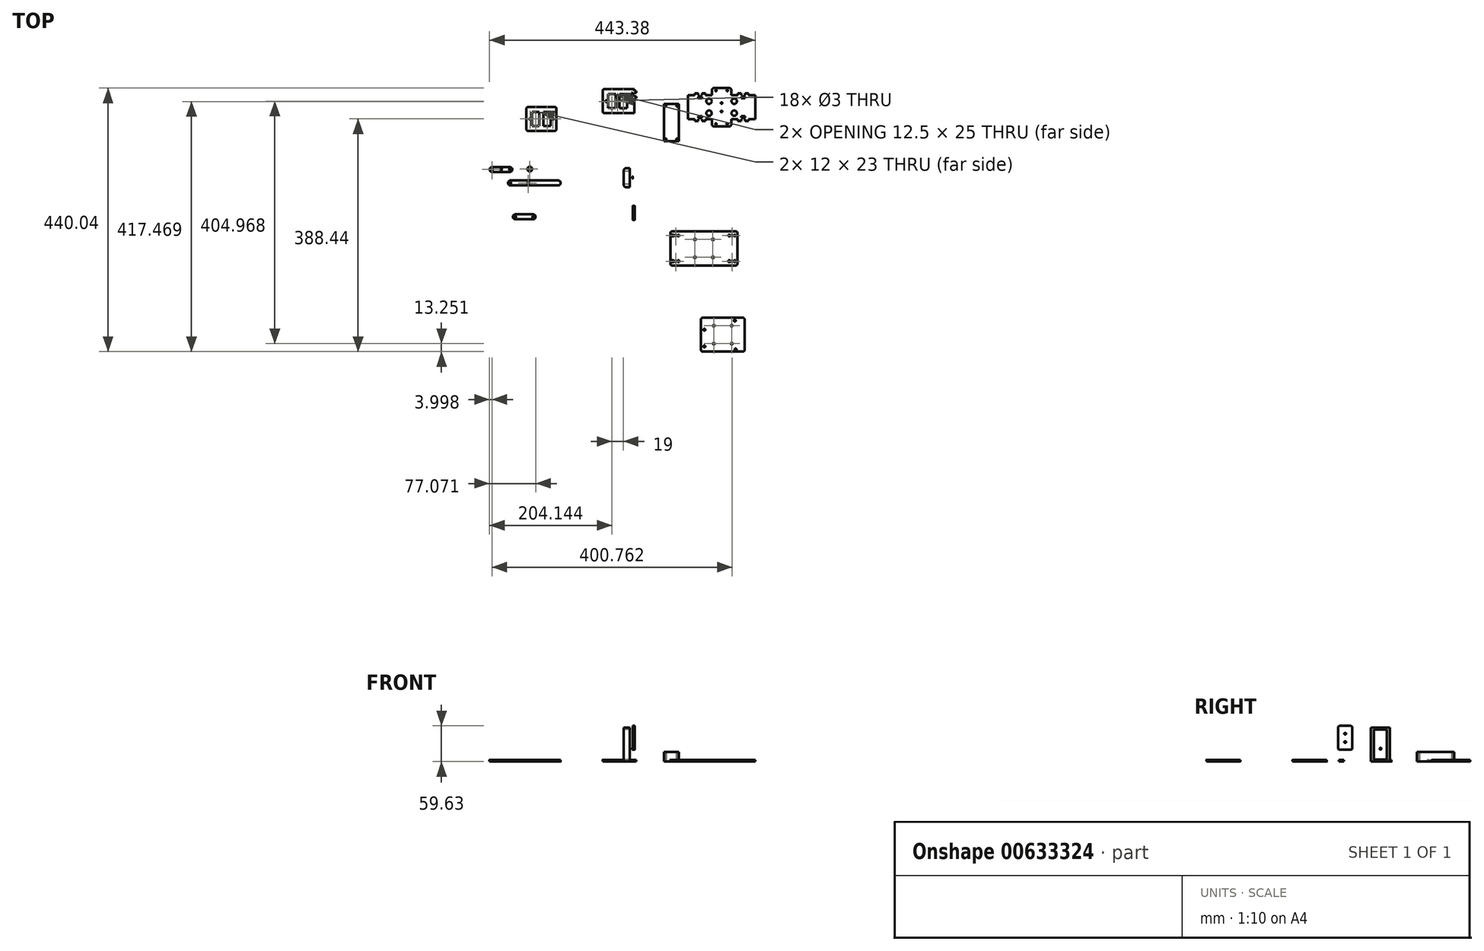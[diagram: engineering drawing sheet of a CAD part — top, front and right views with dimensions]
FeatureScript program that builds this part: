
annotation { "Feature Type Name" : "Feature", "Feature Type Description" : "" }
export const myFeature = defineFeature(function(context is Context, id is Id, definition is map)
    precondition{}
    {
        {
            var Q0;
            Q0=qCreatedBy(makeId("Top.planeOp"),FACE);
            var sketch = newSketch(context, id + "F0", { "sketchPlane" : qUnion([Q0])});
            skCircle(sketch, "E0", {"center": v(29.67, 8.23) * mm, "radius": 4 * mm});
            skCircle(sketch, "E1", {"center": v(29.67, 8.23) * mm, "radius": 1.5 * mm});
            skSolve(sketch);
        }
        {
            var Q0;
            Q0=makeQuery(id+"F0.imprint","IMPRINT",FACE,{"disambiguationData":[TD([[makeQuery(id+"F0.imprint","IMPRINT",EDGE,{"derivedFrom":sQuery(id+"F0.wireOp",EDGE,"E0")}),1.0]])]});
            extrude(context, id + "F1", {"entities" : qUnion([Q0]), "depth" : 3 * mm, "offsetDistance" : 25 * mm});
        }
        {
            var Q0;
            Q0=qCreatedBy(makeId("Top.planeOp"),FACE);
            var sketch = newSketch(context, id + "F2", { "sketchPlane" : qUnion([Q0])});
            skArc(sketch, "E2", {"start": v(-33.45, 11.5) * mm, "mid": v(-37.45, 7.5) * mm, "end": v(-33.45, 3.5) * mm});
            skCircle(sketch, "E3", {"center": v(-33.45, 7.5) * mm, "radius": 1.5 * mm});
            skCircle(sketch, "E4", {"center": v(-3.45, 7.5) * mm, "radius": 1.25 * mm});
            skCircle(sketch, "E5", {"center": v(-18.05, 7.5) * mm, "radius": 1.25 * mm});
            skArc(sketch, "E6", {"start": v(-3.45, 3.5) * mm, "mid": v(0.55, 7.5) * mm, "end": v(-3.45, 11.5) * mm});
            skLineSegment(sketch, "E7", {"start": v(-33.45, 3.5) * mm, "end": v(-3.45, 3.5) * mm});
            skLineSegment(sketch, "E8", {"start": v(-33.45, 11.5) * mm, "end": v(-3.45, 11.5) * mm});
            skSolve(sketch);
        }
        {
            var Q0;
            Q0=makeQuery(id+"F2.imprint","IMPRINT",FACE,{"disambiguationData":[TD([[makeQuery(id+"F2.imprint","IMPRINT",EDGE,{"derivedFrom":sQuery(id+"F2.wireOp",EDGE,"E2")}),1.0]])]});
            extrude(context, id + "F3", {"entities" : qUnion([Q0]), "depth" : 3 * mm, "offsetDistance" : 25 * mm});
        }
        {
            var Q0;
            Q0=qCreatedBy(makeId("Top.planeOp"),FACE);
            var sketch = newSketch(context, id + "F4", { "sketchPlane" : qUnion([Q0])});
            skArc(sketch, "E9", {"start": v(-2.71, -10.96) * mm, "mid": v(-6.71, -14.96) * mm, "end": v(-2.71, -18.96) * mm});
            skCircle(sketch, "E10", {"center": v(-2.71, -14.96) * mm, "radius": 1.3 * mm});
            skLineSegment(sketch, "E11", {"start": v(-2.71, -10.96) * mm, "end": v(77.29, -10.96) * mm});
            skLineSegment(sketch, "E12", {"start": v(-2.71, -18.96) * mm, "end": v(77.29, -18.96) * mm});
            skCircle(sketch, "E13", {"center": v(27.29, -14.96) * mm, "radius": 1.5 * mm});
            skArc(sketch, "E14", {"start": v(77.29, -18.96) * mm, "mid": v(81.29, -14.96) * mm, "end": v(77.29, -10.96) * mm});
            skSolve(sketch);
        }
        {
            var Q0;
            Q0=makeQuery(id+"F4.imprint","IMPRINT",FACE,{"disambiguationData":[TD([[makeQuery(id+"F4.imprint","IMPRINT",EDGE,{"derivedFrom":sQuery(id+"F4.wireOp",EDGE,"E9")}),1.0]])]});
            extrude(context, id + "F5", {"entities" : qUnion([Q0]), "depth" : 3 * mm, "offsetDistance" : 25 * mm});
        }
        {
            var Q0;
            Q0=qCreatedBy(makeId("Top.planeOp"),FACE);
            var sketch = newSketch(context, id + "F6", { "sketchPlane" : qUnion([Q0])});
            skArc(sketch, "E15", {"start": v(5.43, -67.48) * mm, "mid": v(1.43, -71.48) * mm, "end": v(5.43, -75.48) * mm});
            skCircle(sketch, "E16", {"center": v(5.43, -71.48) * mm, "radius": 1.3 * mm});
            skLineSegment(sketch, "E17", {"start": v(5.43, -67.48) * mm, "end": v(35.43, -67.48) * mm});
            skLineSegment(sketch, "E18", {"start": v(5.43, -75.48) * mm, "end": v(35.43, -75.48) * mm});
            skArc(sketch, "E19", {"start": v(35.43, -75.48) * mm, "mid": v(39.43, -71.48) * mm, "end": v(35.43, -67.48) * mm});
            skCircle(sketch, "E20", {"center": v(35.43, -71.48) * mm, "radius": 1.3 * mm});
            skSolve(sketch);
        }
        {
            var Q0;
            Q0=makeQuery(id+"F6.imprint","IMPRINT",FACE,{"disambiguationData":[TD([[makeQuery(id+"F6.imprint","IMPRINT",EDGE,{"derivedFrom":sQuery(id+"F6.wireOp",EDGE,"E15")}),1.0]])]});
            extrude(context, id + "F7", {"entities" : qUnion([Q0]), "depth" : 3 * mm, "offsetDistance" : 25 * mm});
        }
        {
            var Q0;
            Q0=qCreatedBy(makeId("Top.planeOp"),FACE);
            var sketch = newSketch(context, id + "F8", { "sketchPlane" : qUnion([Q0])});
            skLineSegment(sketch, "E21.bottom", {"start": v(33.62, 103.39) * mm, "end": v(45.62, 103.39) * mm});
            skLineSegment(sketch, "E21.top", {"start": v(33.62, 80.39) * mm, "end": v(45.62, 80.39) * mm});
            skLineSegment(sketch, "E21.left", {"start": v(33.62, 103.39) * mm, "end": v(33.62, 80.39) * mm});
            skLineSegment(sketch, "E21.right", {"start": v(45.62, 103.39) * mm, "end": v(45.62, 80.39) * mm});
            skLineSegment(sketch, "E22.MirrorCS", {"start": v(64.62, 103.39) * mm, "end": v(64.62, 80.39) * mm});
            skLineSegment(sketch, "E23.MirrorCS", {"start": v(52.62, 103.39) * mm, "end": v(52.62, 80.39) * mm});
            skLineSegment(sketch, "E24.MirrorCS", {"start": v(64.62, 103.39) * mm, "end": v(52.62, 103.39) * mm});
            skLineSegment(sketch, "E25.MirrorCS", {"start": v(64.62, 80.39) * mm, "end": v(52.62, 80.39) * mm});
            skPoint(sketch, "E26.visualSharp", {"position": v(24.12, 111.89) * mm});
            skPoint(sketch, "E27.visualSharp", {"position": v(74.12, 111.89) * mm});
            skLineSegment(sketch, "E28", {"start": v(27.12, 111.89) * mm, "end": v(71.12, 111.89) * mm});
            skLineSegment(sketch, "E29", {"start": v(74.12, 74.89) * mm, "end": v(74.12, 108.89) * mm});
            skLineSegment(sketch, "E30", {"start": v(24.12, 74.89) * mm, "end": v(24.12, 108.89) * mm});
            skLineSegment(sketch, "E31", {"start": v(27.12, 71.89) * mm, "end": v(71.12, 71.89) * mm});
            skCircle(sketch, "E32", {"center": v(30.12, 91.89) * mm, "radius": 1.5 * mm});
            skPoint(sketch, "E32.centerSnap0", {"position": v(24.12, 91.89) * mm});
            skPoint(sketch, "E33.centerSnap0", {"position": v(45.62, 91.89) * mm});
            skCircle(sketch, "E34", {"center": v(68.12, 91.89) * mm, "radius": 1.5 * mm});
            skPoint(sketch, "E34.centerSnap0", {"position": v(64.62, 91.89) * mm});
            skArc(sketch, "E35.filletArc", {"start": v(27.12, 111.89) * mm, "mid": v(25, 111.01) * mm, "end": v(24.12, 108.89) * mm});
            skArc(sketch, "E36.filletArc", {"start": v(74.12, 108.89) * mm, "mid": v(73.24, 111.01) * mm, "end": v(71.12, 111.89) * mm});
            skPoint(sketch, "E37.visualSharp", {"position": v(74.12, 71.89) * mm});
            skArc(sketch, "E37.filletArc", {"start": v(71.12, 71.89) * mm, "mid": v(73.24, 72.77) * mm, "end": v(74.12, 74.89) * mm});
            skPoint(sketch, "E38.visualSharp", {"position": v(24.12, 71.89) * mm});
            skArc(sketch, "E38.filletArc", {"start": v(24.12, 74.89) * mm, "mid": v(25, 72.77) * mm, "end": v(27.12, 71.89) * mm});
            skSolve(sketch);
        }
        {
            var Q0;
            Q0=makeQuery(id+"F8.imprint","IMPRINT",FACE,{"disambiguationData":[TD([[makeQuery(id+"F8.imprint","IMPRINT",EDGE,{"derivedFrom":sQuery(id+"F8.wireOp",EDGE,"E21.bottom")}),1.0]])]});
            extrude(context, id + "F9", {"entities" : qUnion([Q0]), "depth" : 3 * mm, "offsetDistance" : 25 * mm});
        }
        {
            var Q0;
            Q0=qCreatedBy(makeId("Top.planeOp"),FACE);
            var sketch = newSketch(context, id + "F10", { "sketchPlane" : qUnion([Q0])});
            skLineSegment(sketch, "E39.bottom", {"start": v(191.16, 9.78) * mm, "end": v(201.86, 9.78) * mm});
            skLineSegment(sketch, "E39.top", {"start": v(191.16, -22.22) * mm, "end": v(201.86, -22.22) * mm});
            skLineSegment(sketch, "E39.left", {"start": v(186.16, 4.78) * mm, "end": v(186.16, -17.22) * mm});
            skLineSegment(sketch, "E39.right", {"start": v(201.86, 9.78) * mm, "end": v(201.86, -22.22) * mm});
            skPoint(sketch, "E40.visualSharp", {"position": v(186.16, 9.78) * mm});
            skArc(sketch, "E40.filletArc", {"start": v(191.16, 9.78) * mm, "mid": v(187.62, 8.31) * mm, "end": v(186.16, 4.78) * mm});
            skPoint(sketch, "E41.visualSharp", {"position": v(186.16, -22.22) * mm});
            skArc(sketch, "E41.filletArc", {"start": v(186.16, -17.22) * mm, "mid": v(187.62, -20.76) * mm, "end": v(191.16, -22.22) * mm});
            skSolve(sketch);
        }
        {
            var Q0;
            Q0=makeQuery(id+"F10.imprint","IMPRINT",FACE,{"disambiguationData":[TD([[makeQuery(id+"F10.imprint","IMPRINT",EDGE,{"derivedFrom":sQuery(id+"F10.wireOp",EDGE,"E39.bottom")}),-1.0]])]});
            extrude(context, id + "F11", {"entities" : qUnion([Q0]), "depth" : 57 * mm, "offsetDistance" : 25 * mm});
        }
        {
            var Q0;
            Q0=makeQuery(id+"F11.opExtrude","SWEPT_FACE",FACE,{"disambiguationData":[OSD([sQuery(id+"F10.wireOp",EDGE,"E39.right")])]});
            var sketch = newSketch(context, id + "F12", { "sketchPlane" : qUnion([Q0])});
            skPoint(sketch, "E42.endSnap0", {"position": v(9.78, 28.5) * mm});
            skCircle(sketch, "E43", {"center": v(-5.9, 35.5) * mm, "radius": 1.4 * mm});
            skPoint(sketch, "E43.centerSnap0", {"position": v(-5.9, 28.5) * mm});
            skCircle(sketch, "E44.MirrorC", {"center": v(-5.9, 21.5) * mm, "radius": 1.4 * mm});
            skSolve(sketch);
        }
        {
            var Q0;
            Q0=makeQuery(id+"F12.imprint","IMPRINT",FACE,{"disambiguationData":[TD([[makeQuery(id+"F12.imprint","IMPRINT",EDGE,{"derivedFrom":sQuery(id+"F12.wireOp",EDGE,"E43")}),1.0]])]});
            var Q1;
            Q1=makeQuery(id+"F12.imprint","IMPRINT",FACE,{"disambiguationData":[TD([[makeQuery(id+"F12.imprint","IMPRINT",EDGE,{"derivedFrom":sQuery(id+"F12.wireOp",EDGE,"E44.MirrorC")}),-1.0]])]});
            extrude(context, id + "F13", {"entities" : qUnion([Q0, Q1]), "operationType" : NewBodyOperationType.REMOVE, "oppositeDirection" : true, "depth" : 5 * mm, "offsetDistance" : 25 * mm});
        }
        {
            var Q0;
            Q0=qCreatedBy(makeId("Top.planeOp"),FACE);
            var sketch = newSketch(context, id + "F14", { "sketchPlane" : qUnion([Q0])});
            skLineSegment(sketch, "E45.bottom", {"start": v(-78.5, 126.14) * mm, "end": v(-53.3, 126.14) * mm});
            skLineSegment(sketch, "E45.top", {"start": v(-78.5, 63.74) * mm, "end": v(-53.3, 63.74) * mm});
            skLineSegment(sketch, "E45.left", {"start": v(-78.5, 126.14) * mm, "end": v(-78.5, 63.74) * mm});
            skLineSegment(sketch, "E45.right", {"start": v(-53.3, 126.14) * mm, "end": v(-53.3, 63.74) * mm});
            skCircle(sketch, "E46", {"center": v(-75.35, 122.84) * mm, "radius": 1.2 * mm});
            skCircle(sketch, "E47", {"center": v(-56.45, 122.84) * mm, "radius": 1.2 * mm});
            skCircle(sketch, "E48", {"center": v(-75.35, 67.04) * mm, "radius": 1.2 * mm});
            skCircle(sketch, "E49", {"center": v(-56.45, 67.04) * mm, "radius": 1.2 * mm});
            skSolve(sketch);
        }
        {
            var Q0;
            Q0=makeQuery(id+"F14.imprint","IMPRINT",FACE,{"disambiguationData":[TD([[makeQuery(id+"F14.imprint","IMPRINT",EDGE,{"derivedFrom":sQuery(id+"F14.wireOp",EDGE,"E45.bottom")}),-1.0]])]});
            extrude(context, id + "F15", {"entities" : qUnion([Q0]), "depth" : 15.8 * mm, "offsetDistance" : 25 * mm});
        }
        {
            var Q0;
            Q0=qCreatedBy(makeId("Top.planeOp"),FACE);
            var sketch = newSketch(context, id + "F16", { "sketchPlane" : qUnion([Q0])});
            skPoint(sketch, "E50.visualSharp", {"position": v(151.2, 141.67) * mm});
            skPoint(sketch, "E51.visualSharp", {"position": v(204.44, 141.67) * mm});
            skLineSegment(sketch, "E52", {"start": v(154.2, 141.67) * mm, "end": v(204.44, 141.67) * mm});
            skLineSegment(sketch, "E53", {"start": v(151.2, 104.67) * mm, "end": v(151.2, 138.67) * mm});
            skLineSegment(sketch, "E54", {"start": v(154.2, 101.67) * mm, "end": v(204.2, 101.67) * mm});
            skCircle(sketch, "E55", {"center": v(157.2, 121.67) * mm, "radius": 1.3 * mm});
            skPoint(sketch, "E55.centerSnap0", {"position": v(151.2, 121.67) * mm});
            skArc(sketch, "E56.filletArc", {"start": v(154.2, 141.67) * mm, "mid": v(152.07, 140.8) * mm, "end": v(151.2, 138.67) * mm});
            skPoint(sketch, "E57.visualSharp", {"position": v(204.2, 101.67) * mm});
            skPoint(sketch, "E58.visualSharp", {"position": v(151.2, 101.67) * mm});
            skArc(sketch, "E58.filletArc", {"start": v(151.2, 104.67) * mm, "mid": v(152.07, 102.55) * mm, "end": v(154.2, 101.67) * mm});
            skCircle(sketch, "E59", {"center": v(176.2, 121.67) * mm, "radius": 1.5 * mm});
            skLineSegment(sketch, "E60.bottom", {"start": v(174.7, 118.67) * mm, "end": v(177.7, 118.67) * mm});
            skLineSegment(sketch, "E60.top", {"start": v(174.7, 112.67) * mm, "end": v(177.7, 112.67) * mm});
            skLineSegment(sketch, "E60.left", {"start": v(174.7, 118.67) * mm, "end": v(174.7, 112.67) * mm});
            skLineSegment(sketch, "E60.right", {"start": v(177.7, 118.67) * mm, "end": v(177.7, 112.67) * mm});
            skPoint(sketch, "E61", {"position": v(176.2, 118.67) * mm});
            skLineSegment(sketch, "E62.MirrorCS", {"start": v(201.7, 134.15) * mm, "end": v(204.2, 134.15) * mm});
            skLineSegment(sketch, "E63.MirrorCS", {"start": v(204.2, 134.15) * mm, "end": v(204.2, 135.67) * mm});
            skLineSegment(sketch, "E64.MirrorCS", {"start": v(207.2, 138.67) * mm, "end": v(204.44, 138.67) * mm});
            skLineSegment(sketch, "E65.MirrorCS", {"start": v(204.2, 135.67) * mm, "end": v(207.2, 135.67) * mm});
            skLineSegment(sketch, "E66.MirrorCS", {"start": v(199.2, 135.67) * mm, "end": v(201.7, 135.67) * mm});
            skLineSegment(sketch, "E67.MirrorCS", {"start": v(199.2, 129.67) * mm, "end": v(201.7, 129.67) * mm});
            skLineSegment(sketch, "E68.MirrorCS", {"start": v(201.7, 129.67) * mm, "end": v(201.7, 131.19) * mm});
            skLineSegment(sketch, "E69.MirrorCS", {"start": v(201.7, 135.67) * mm, "end": v(201.7, 134.15) * mm});
            skLineSegment(sketch, "E70.MirrorCS", {"start": v(207.2, 126.67) * mm, "end": v(204.2, 126.67) * mm});
            skLineSegment(sketch, "E71.MirrorCS", {"start": v(204.2, 131.19) * mm, "end": v(204.2, 129.67) * mm});
            skLineSegment(sketch, "E72.MirrorCS", {"start": v(201.7, 131.19) * mm, "end": v(204.2, 131.19) * mm});
            skLineSegment(sketch, "E73.MirrorCS", {"start": v(204.2, 129.67) * mm, "end": v(207.2, 129.67) * mm});
            skLineSegment(sketch, "E74.MirrorCS", {"start": v(207.2, 135.67) * mm, "end": v(207.2, 138.67) * mm});
            skLineSegment(sketch, "E75.MirrorCS", {"start": v(207.2, 129.67) * mm, "end": v(207.2, 126.67) * mm});
            skPoint(sketch, "E76", {"position": v(204.44, 138.67) * mm});
            skLineSegment(sketch, "E77", {"start": v(204.2, 101.67) * mm, "end": v(204.2, 126.67) * mm});
            skLineSegment(sketch, "E78", {"start": v(204.44, 138.67) * mm, "end": v(204.44, 141.67) * mm});
            skLineSegment(sketch, "E79", {"start": v(176.2, 101.67) * mm, "end": v(176.2, 141.67) * mm, "construction": true});
            skPoint(sketch, "E79.startSnap0", {"position": v(176.2, 112.67) * mm});
            skLineSegment(sketch, "E80.bottom", {"start": v(160.7, 133.17) * mm, "end": v(172.7, 133.17) * mm, "construction": true});
            skLineSegment(sketch, "E80.top", {"start": v(160.7, 110.17) * mm, "end": v(172.7, 110.17) * mm, "construction": true});
            skLineSegment(sketch, "E80.left", {"start": v(160.7, 133.17) * mm, "end": v(160.7, 110.17) * mm, "construction": true});
            skLineSegment(sketch, "E80.right", {"start": v(172.7, 133.17) * mm, "end": v(172.7, 110.17) * mm, "construction": true});
            skPoint(sketch, "E81.centerSnap0", {"position": v(172.7, 121.67) * mm});
            skLineSegment(sketch, "E82", {"start": v(151.2, 121.67) * mm, "end": v(201.2, 121.67) * mm, "construction": true});
            skLineSegment(sketch, "E83.0", {"start": v(160.44, 133.42) * mm, "end": v(172.94, 133.42) * mm});
            skLineSegment(sketch, "E83.1", {"start": v(160.44, 133.42) * mm, "end": v(160.44, 109.92) * mm});
            skLineSegment(sketch, "E83.2", {"start": v(160.44, 109.92) * mm, "end": v(165.2, 109.92) * mm});
            skLineSegment(sketch, "E83.3", {"start": v(172.94, 133.42) * mm, "end": v(172.94, 109.92) * mm});
            skLineSegment(sketch, "E84.MirrorCS", {"start": v(177.7, 124.67) * mm, "end": v(177.7, 130.67) * mm});
            skPoint(sketch, "E85.MirrorP", {"position": v(176.2, 124.67) * mm});
            skLineSegment(sketch, "E86.MirrorCS", {"start": v(174.7, 124.67) * mm, "end": v(174.7, 130.67) * mm});
            skLineSegment(sketch, "E87.MirrorCS", {"start": v(174.7, 124.67) * mm, "end": v(177.7, 124.67) * mm});
            skLineSegment(sketch, "E88.MirrorCS", {"start": v(174.7, 130.67) * mm, "end": v(177.7, 130.67) * mm});
            skPoint(sketch, "E89.MirrorP", {"position": v(176.2, 130.67) * mm});
            skArc(sketch, "E90", {"start": v(165.2, 109.92) * mm, "mid": v(166.7, 108.42) * mm, "end": v(168.2, 109.92) * mm});
            skLineSegment(sketch, "E91.trimOffspring", {"start": v(168.2, 109.92) * mm, "end": v(172.94, 109.92) * mm});
            skLineSegment(sketch, "E92.MirrorCS", {"start": v(191.7, 133.17) * mm, "end": v(179.7, 133.17) * mm, "construction": true});
            skLineSegment(sketch, "E93.MirrorCS", {"start": v(191.7, 133.17) * mm, "end": v(191.7, 110.17) * mm, "construction": true});
            skLineSegment(sketch, "E94.MirrorCS", {"start": v(191.94, 133.42) * mm, "end": v(191.94, 109.92) * mm});
            skLineSegment(sketch, "E95.MirrorCS", {"start": v(179.7, 133.17) * mm, "end": v(179.7, 110.17) * mm, "construction": true});
            skLineSegment(sketch, "E96.MirrorCS", {"start": v(191.7, 110.17) * mm, "end": v(179.7, 110.17) * mm, "construction": true});
            skLineSegment(sketch, "E97.MirrorCS", {"start": v(191.94, 109.92) * mm, "end": v(187.2, 109.92) * mm});
            skPoint(sketch, "E98.MirrorP", {"position": v(179.7, 121.67) * mm});
            skCircle(sketch, "E99.MirrorC", {"center": v(195.2, 121.67) * mm, "radius": 1.3 * mm});
            skLineSegment(sketch, "E100.MirrorCS", {"start": v(191.94, 133.42) * mm, "end": v(179.44, 133.42) * mm});
            skArc(sketch, "E101.MirrorCS", {"start": v(187.2, 109.92) * mm, "mid": v(185.7, 108.42) * mm, "end": v(184.2, 109.92) * mm});
            skLineSegment(sketch, "E102.MirrorCS", {"start": v(184.2, 109.92) * mm, "end": v(179.44, 109.92) * mm});
            skLineSegment(sketch, "E103.MirrorCS", {"start": v(179.44, 133.42) * mm, "end": v(179.44, 109.92) * mm});
            skLineSegment(sketch, "E104", {"start": v(199.2, 135.67) * mm, "end": v(199.2, 129.67) * mm});
            skSolve(sketch);
        }
        {
            var Q0;
            Q0=makeQuery(id+"F16.imprint","IMPRINT",FACE,{"disambiguationData":[TD([[makeQuery(id+"F16.imprint","IMPRINT",EDGE,{"derivedFrom":sQuery(id+"F16.wireOp",EDGE,"E52")}),-1.0]])]});
            extrude(context, id + "F17", {"entities" : qUnion([Q0]), "depth" : 3 * mm, "offsetDistance" : 25 * mm});
        }
        {
            var Q0;
            Q0=qCreatedBy(makeId("Top.planeOp"),FACE);
            var sketch = newSketch(context, id + "F18", { "sketchPlane" : qUnion([Q0])});
            skPoint(sketch, "E105.endSnap0", {"position": v(293.93, 111.5) * mm});
            skPoint(sketch, "E106.MirrorP", {"position": v(293.93, 91.5) * mm});
            skLineSegment(sketch, "E107.MirrorCS", {"start": v(293.93, 111.5) * mm, "end": v(293.93, 91.5) * mm});
            skCircle(sketch, "E108", {"center": v(340.48, 83.6) * mm, "radius": 1.2 * mm});
            skCircle(sketch, "E109.MirrorC", {"center": v(349.93, 104.5) * mm, "radius": 1.3 * mm});
            skPoint(sketch, "E110", {"position": v(349.93, 111.5) * mm});
            skCircle(sketch, "E111", {"center": v(328.93, 101.5) * mm, "radius": 4.5 * mm});
            skLineSegment(sketch, "E112", {"start": v(349.93, 79.5) * mm, "end": v(349.93, 143.48) * mm, "construction": true});
            skLineSegment(sketch, "E113", {"start": v(293.93, 111.5) * mm, "end": v(349.93, 111.5) * mm, "construction": true});
            skCircle(sketch, "E114.MirrorC", {"center": v(349.93, 118.5) * mm, "radius": 1.3 * mm});
            skLineSegment(sketch, "E115.MirrorCS", {"start": v(293.93, 91.5) * mm, "end": v(304.93, 91.5) * mm});
            skLineSegment(sketch, "E116.MirrorCS", {"start": v(322.93, 91.5) * mm, "end": v(333.93, 91.5) * mm});
            skLineSegment(sketch, "E117.MirrorCS", {"start": v(312.44, 91.5) * mm, "end": v(310.93, 91.5) * mm});
            skLineSegment(sketch, "E118.MirrorCS", {"start": v(316.93, 94) * mm, "end": v(315.4, 94) * mm});
            skLineSegment(sketch, "E119.MirrorCS", {"start": v(310.93, 94) * mm, "end": v(312.44, 94) * mm});
            skLineSegment(sketch, "E120.MirrorCS", {"start": v(315.4, 91.5) * mm, "end": v(316.93, 91.5) * mm});
            skLineSegment(sketch, "E121.MirrorCS", {"start": v(312.44, 94) * mm, "end": v(312.44, 91.5) * mm});
            skLineSegment(sketch, "E122.MirrorCS", {"start": v(310.93, 91.5) * mm, "end": v(310.93, 88.5) * mm});
            skLineSegment(sketch, "E123.MirrorCS", {"start": v(316.93, 96.5) * mm, "end": v(316.93, 94) * mm});
            skLineSegment(sketch, "E124.MirrorCS", {"start": v(304.93, 88.5) * mm, "end": v(304.93, 91.5) * mm});
            skLineSegment(sketch, "E125.MirrorCS", {"start": v(322.93, 88.5) * mm, "end": v(322.93, 91.5) * mm});
            skLineSegment(sketch, "E126.MirrorCS", {"start": v(316.93, 91.5) * mm, "end": v(316.93, 88.5) * mm});
            skLineSegment(sketch, "E127.MirrorCS", {"start": v(310.93, 96.5) * mm, "end": v(310.93, 94) * mm});
            skLineSegment(sketch, "E128.MirrorCS", {"start": v(315.4, 94) * mm, "end": v(315.4, 91.5) * mm});
            skLineSegment(sketch, "E129.MirrorCS", {"start": v(316.93, 88.5) * mm, "end": v(322.93, 88.5) * mm});
            skLineSegment(sketch, "E130.MirrorCS", {"start": v(310.93, 96.5) * mm, "end": v(316.93, 96.5) * mm});
            skLineSegment(sketch, "E131.MirrorCS", {"start": v(310.93, 88.5) * mm, "end": v(304.93, 88.5) * mm});
            skPoint(sketch, "E132.positionSnap0", {"position": v(313.93, 96.5) * mm});
            skLineSegment(sketch, "E133", {"start": v(333.93, 91.5) * mm, "end": v(333.93, 82.5) * mm});
            skLineSegment(sketch, "E134", {"start": v(336.93, 79.5) * mm, "end": v(349.93, 79.5) * mm});
            skPoint(sketch, "E135.visualSharp", {"position": v(333.93, 79.5) * mm});
            skArc(sketch, "E135.filletArc", {"start": v(333.93, 82.5) * mm, "mid": v(334.8, 80.38) * mm, "end": v(336.93, 79.5) * mm});
            skLineSegment(sketch, "E136.MirrorCS", {"start": v(315.4, 129) * mm, "end": v(315.4, 131.5) * mm});
            skLineSegment(sketch, "E137.MirrorCS", {"start": v(316.93, 129) * mm, "end": v(315.4, 129) * mm});
            skLineSegment(sketch, "E138.MirrorCS", {"start": v(315.4, 131.5) * mm, "end": v(316.93, 131.5) * mm});
            skLineSegment(sketch, "E139.MirrorCS", {"start": v(310.93, 131.5) * mm, "end": v(310.93, 134.5) * mm});
            skLineSegment(sketch, "E140.MirrorCS", {"start": v(304.93, 134.5) * mm, "end": v(304.93, 131.5) * mm});
            skLineSegment(sketch, "E141.MirrorCS", {"start": v(310.93, 129) * mm, "end": v(312.44, 129) * mm});
            skLineSegment(sketch, "E142.MirrorCS", {"start": v(312.44, 129) * mm, "end": v(312.44, 131.5) * mm});
            skLineSegment(sketch, "E143.MirrorCS", {"start": v(312.44, 131.5) * mm, "end": v(310.93, 131.5) * mm});
            skLineSegment(sketch, "E144.MirrorCS", {"start": v(316.93, 131.5) * mm, "end": v(316.93, 134.5) * mm});
            skLineSegment(sketch, "E145.MirrorCS", {"start": v(322.93, 134.5) * mm, "end": v(322.93, 131.5) * mm});
            skLineSegment(sketch, "E146.MirrorCS", {"start": v(316.93, 126.5) * mm, "end": v(316.93, 129) * mm});
            skLineSegment(sketch, "E147.MirrorCS", {"start": v(310.93, 126.5) * mm, "end": v(310.93, 129) * mm});
            skArc(sketch, "E148.MirrorCS", {"start": v(333.93, 140.5) * mm, "mid": v(334.8, 142.61) * mm, "end": v(336.93, 143.5) * mm});
            skLineSegment(sketch, "E149.MirrorCS", {"start": v(316.93, 134.5) * mm, "end": v(322.93, 134.5) * mm});
            skCircle(sketch, "E150.MirrorC", {"center": v(340.48, 139.4) * mm, "radius": 1.2 * mm});
            skPoint(sketch, "E151.MirrorP", {"position": v(293.93, 131.5) * mm});
            skLineSegment(sketch, "E152.MirrorCS", {"start": v(310.93, 126.5) * mm, "end": v(316.93, 126.5) * mm});
            skLineSegment(sketch, "E153.MirrorCS", {"start": v(333.93, 131.5) * mm, "end": v(333.93, 140.5) * mm});
            skCircle(sketch, "E154.MirrorC", {"center": v(328.93, 121.5) * mm, "radius": 4.5 * mm});
            skLineSegment(sketch, "E155.MirrorCS", {"start": v(293.93, 111.5) * mm, "end": v(293.93, 131.5) * mm});
            skLineSegment(sketch, "E156.MirrorCS", {"start": v(322.93, 131.5) * mm, "end": v(333.93, 131.5) * mm});
            skLineSegment(sketch, "E157.MirrorCS", {"start": v(336.93, 143.5) * mm, "end": v(349.93, 143.5) * mm});
            skPoint(sketch, "E158.MirrorP", {"position": v(333.93, 143.5) * mm});
            skPoint(sketch, "E159.MirrorP", {"position": v(313.93, 126.5) * mm});
            skLineSegment(sketch, "E160.MirrorCS", {"start": v(310.93, 134.5) * mm, "end": v(304.93, 134.5) * mm});
            skLineSegment(sketch, "E161.MirrorCS", {"start": v(293.93, 131.5) * mm, "end": v(304.93, 131.5) * mm});
            skPoint(sketch, "E162.MirrorP", {"position": v(405.93, 111.5) * mm});
            skLineSegment(sketch, "E163.MirrorCS", {"start": v(382.93, 129) * mm, "end": v(384.44, 129) * mm});
            skLineSegment(sketch, "E164.MirrorCS", {"start": v(387.4, 131.5) * mm, "end": v(388.93, 131.5) * mm});
            skLineSegment(sketch, "E165.MirrorCS", {"start": v(384.44, 94) * mm, "end": v(384.44, 91.5) * mm});
            skLineSegment(sketch, "E166.MirrorCS", {"start": v(382.93, 94) * mm, "end": v(384.44, 94) * mm});
            skLineSegment(sketch, "E167.MirrorCS", {"start": v(388.93, 131.5) * mm, "end": v(388.93, 134.5) * mm});
            skArc(sketch, "E168.MirrorCS", {"start": v(365.93, 140.5) * mm, "mid": v(365.05, 142.61) * mm, "end": v(362.93, 143.5) * mm});
            skLineSegment(sketch, "E169.MirrorCS", {"start": v(388.93, 94) * mm, "end": v(387.4, 94) * mm});
            skLineSegment(sketch, "E170.MirrorCS", {"start": v(384.44, 91.5) * mm, "end": v(382.93, 91.5) * mm});
            skLineSegment(sketch, "E171.MirrorCS", {"start": v(376.93, 88.5) * mm, "end": v(376.93, 91.5) * mm});
            skLineSegment(sketch, "E172.MirrorCS", {"start": v(387.4, 91.5) * mm, "end": v(388.93, 91.5) * mm});
            skLineSegment(sketch, "E173.MirrorCS", {"start": v(387.4, 94) * mm, "end": v(387.4, 91.5) * mm});
            skLineSegment(sketch, "E174.MirrorCS", {"start": v(394.93, 134.5) * mm, "end": v(394.93, 131.5) * mm});
            skLineSegment(sketch, "E175.MirrorCS", {"start": v(376.93, 134.5) * mm, "end": v(376.93, 131.5) * mm});
            skLineSegment(sketch, "E176.MirrorCS", {"start": v(382.93, 131.5) * mm, "end": v(382.93, 134.5) * mm});
            skLineSegment(sketch, "E177.MirrorCS", {"start": v(388.93, 126.5) * mm, "end": v(388.93, 129) * mm});
            skLineSegment(sketch, "E178.MirrorCS", {"start": v(382.93, 91.5) * mm, "end": v(382.93, 88.5) * mm});
            skLineSegment(sketch, "E179.MirrorCS", {"start": v(388.93, 129) * mm, "end": v(387.4, 129) * mm});
            skLineSegment(sketch, "E180.MirrorCS", {"start": v(384.44, 129) * mm, "end": v(384.44, 131.5) * mm});
            skArc(sketch, "E181.MirrorCS", {"start": v(365.93, 82.5) * mm, "mid": v(365.05, 80.38) * mm, "end": v(362.93, 79.5) * mm});
            skLineSegment(sketch, "E182.MirrorCS", {"start": v(382.93, 126.5) * mm, "end": v(382.93, 129) * mm});
            skLineSegment(sketch, "E183.MirrorCS", {"start": v(387.4, 129) * mm, "end": v(387.4, 131.5) * mm});
            skLineSegment(sketch, "E184.MirrorCS", {"start": v(388.93, 96.5) * mm, "end": v(388.93, 94) * mm});
            skLineSegment(sketch, "E185.MirrorCS", {"start": v(384.44, 131.5) * mm, "end": v(382.93, 131.5) * mm});
            skLineSegment(sketch, "E186.MirrorCS", {"start": v(388.93, 91.5) * mm, "end": v(388.93, 88.5) * mm});
            skLineSegment(sketch, "E187.MirrorCS", {"start": v(394.93, 88.5) * mm, "end": v(394.93, 91.5) * mm});
            skLineSegment(sketch, "E188.MirrorCS", {"start": v(382.93, 96.5) * mm, "end": v(382.93, 94) * mm});
            skPoint(sketch, "E189.MirrorP", {"position": v(405.93, 91.5) * mm});
            skCircle(sketch, "E190.MirrorC", {"center": v(359.38, 83.6) * mm, "radius": 1.2 * mm});
            skPoint(sketch, "E191.MirrorP", {"position": v(405.93, 131.5) * mm});
            skLineSegment(sketch, "E192.MirrorCS", {"start": v(382.93, 88.5) * mm, "end": v(376.93, 88.5) * mm});
            skLineSegment(sketch, "E193.MirrorCS", {"start": v(388.93, 96.5) * mm, "end": v(382.93, 96.5) * mm});
            skLineSegment(sketch, "E194.MirrorCS", {"start": v(388.93, 126.5) * mm, "end": v(382.93, 126.5) * mm});
            skCircle(sketch, "E195.MirrorC", {"center": v(359.38, 139.4) * mm, "radius": 1.2 * mm});
            skPoint(sketch, "E196.MirrorP", {"position": v(385.93, 126.5) * mm});
            skLineSegment(sketch, "E197.MirrorCS", {"start": v(365.93, 91.5) * mm, "end": v(365.93, 82.5) * mm});
            skLineSegment(sketch, "E198.MirrorCS", {"start": v(405.93, 111.5) * mm, "end": v(405.93, 91.5) * mm});
            skPoint(sketch, "E199.MirrorP", {"position": v(365.93, 143.5) * mm});
            skCircle(sketch, "E200.MirrorC", {"center": v(370.93, 121.5) * mm, "radius": 4.5 * mm});
            skLineSegment(sketch, "E201.MirrorCS", {"start": v(365.93, 131.5) * mm, "end": v(365.93, 140.5) * mm});
            skLineSegment(sketch, "E202.MirrorCS", {"start": v(382.93, 134.5) * mm, "end": v(376.93, 134.5) * mm});
            skCircle(sketch, "E203.MirrorC", {"center": v(370.93, 101.5) * mm, "radius": 4.5 * mm});
            skLineSegment(sketch, "E204.MirrorCS", {"start": v(405.93, 111.5) * mm, "end": v(405.93, 131.5) * mm});
            skLineSegment(sketch, "E205.MirrorCS", {"start": v(405.93, 91.5) * mm, "end": v(394.93, 91.5) * mm});
            skPoint(sketch, "E206.MirrorP", {"position": v(365.93, 79.5) * mm});
            skPoint(sketch, "E207.MirrorP", {"position": v(385.93, 96.5) * mm});
            skLineSegment(sketch, "E208.MirrorCS", {"start": v(388.93, 88.5) * mm, "end": v(394.93, 88.5) * mm});
            skLineSegment(sketch, "E209.MirrorCS", {"start": v(362.93, 79.5) * mm, "end": v(349.93, 79.5) * mm});
            skLineSegment(sketch, "E210.MirrorCS", {"start": v(388.93, 134.5) * mm, "end": v(394.93, 134.5) * mm});
            skLineSegment(sketch, "E211.MirrorCS", {"start": v(376.93, 131.5) * mm, "end": v(365.93, 131.5) * mm});
            skLineSegment(sketch, "E212.MirrorCS", {"start": v(362.93, 143.5) * mm, "end": v(349.93, 143.5) * mm});
            skLineSegment(sketch, "E213.MirrorCS", {"start": v(376.93, 91.5) * mm, "end": v(365.93, 91.5) * mm});
            skLineSegment(sketch, "E214.MirrorCS", {"start": v(405.93, 131.5) * mm, "end": v(394.93, 131.5) * mm});
            skSolve(sketch);
        }
        {
            var Q0;
            Q0=makeQuery(id+"F18.imprint","IMPRINT",FACE,{"disambiguationData":[TD([[makeQuery(id+"F18.imprint","IMPRINT",EDGE,{"derivedFrom":sQuery(id+"F18.wireOp",EDGE,"E107.MirrorCS")}),1.0]])]});
            extrude(context, id + "F19", {"entities" : qUnion([Q0]), "depth" : 3 * mm, "offsetDistance" : 25 * mm});
        }
        {
            var Q0;
            Q0=makeQuery(id+"F15.opExtrude","SWEPT_BODY",BODY,{"disambiguationData":[OSD([sQuery(id+"F14.wireOp",EDGE,"E45.bottom"),sQuery(id+"F14.wireOp",EDGE,"E45.top"),sQuery(id+"F14.wireOp",EDGE,"E45.left"),sQuery(id+"F14.wireOp",EDGE,"E45.right"),sQuery(id+"F14.wireOp",EDGE,"E46"),sQuery(id+"F14.wireOp",EDGE,"E47"),sQuery(id+"F14.wireOp",EDGE,"E48"),sQuery(id+"F14.wireOp",EDGE,"E49")])]});
            transform(context, id + "F20", {"entities" : qUnion([Q0]), "transformType" : TransformType.TRANSLATION_3D, "dx" : 332 * mm, "dy" : -9 * mm, "dz" : 0 * mm, "makeCopy" : false});
        }
        {
            var Q0;
            Q0=makeQuery(id+"F11.opExtrude","SWEPT_FACE",FACE,{"disambiguationData":[OSD([sQuery(id+"F10.wireOp",EDGE,"E39.right")])]});
            var sketch = newSketch(context, id + "F21", { "sketchPlane" : qUnion([Q0])});
            skCircle(sketch, "E215", {"center": v(-64.97, 46.63) * mm, "radius": 1.5 * mm});
            skPoint(sketch, "E215.centerSnap0", {"position": v(-64.97, 39.63) * mm});
            skCircle(sketch, "E216.MirrorC", {"center": v(-64.97, 32.63) * mm, "radius": 1.5 * mm});
            skLineSegment(sketch, "E217.bottom", {"start": v(-73.97, 59.63) * mm, "end": v(-55.97, 59.63) * mm});
            skLineSegment(sketch, "E217.top", {"start": v(-73.97, 19.63) * mm, "end": v(-55.97, 19.63) * mm});
            skLineSegment(sketch, "E217.left", {"start": v(-76.97, 56.63) * mm, "end": v(-76.97, 22.63) * mm});
            skLineSegment(sketch, "E217.right", {"start": v(-52.97, 56.63) * mm, "end": v(-52.97, 22.63) * mm});
            skPoint(sketch, "E218.visualSharp", {"position": v(-52.97, 59.63) * mm});
            skArc(sketch, "E218.filletArc", {"start": v(-52.97, 56.63) * mm, "mid": v(-53.85, 58.75) * mm, "end": v(-55.97, 59.63) * mm});
            skPoint(sketch, "E219.visualSharp", {"position": v(-76.97, 59.63) * mm});
            skArc(sketch, "E219.filletArc", {"start": v(-73.97, 59.63) * mm, "mid": v(-76.1, 58.75) * mm, "end": v(-76.97, 56.63) * mm});
            skPoint(sketch, "E220.visualSharp", {"position": v(-52.97, 19.63) * mm});
            skArc(sketch, "E220.filletArc", {"start": v(-55.97, 19.63) * mm, "mid": v(-53.85, 20.5) * mm, "end": v(-52.97, 22.63) * mm});
            skPoint(sketch, "E221.visualSharp", {"position": v(-76.97, 19.63) * mm});
            skArc(sketch, "E221.filletArc", {"start": v(-76.97, 22.63) * mm, "mid": v(-76.1, 20.5) * mm, "end": v(-73.97, 19.63) * mm});
            skSolve(sketch);
        }
        {
            var Q0;
            Q0=makeQuery(id+"F21.imprint","IMPRINT",FACE,{"disambiguationData":[TD([[makeQuery(id+"F21.imprint","IMPRINT",EDGE,{"derivedFrom":sQuery(id+"F21.wireOp",EDGE,"E215")}),-1.0]])]});
            extrude(context, id + "F22", {"entities" : qUnion([Q0]), "depth" : 3 * mm, "offsetDistance" : 25 * mm});
        }
        {
            var Q0;
            Q0=makeQuery(id+"F11.opExtrude","SWEPT_FACE",FACE,{"disambiguationData":[OSD([sQuery(id+"F10.wireOp",EDGE,"E39.left")])]});
            var sketch = newSketch(context, id + "F23", { "sketchPlane" : qUnion([Q0])});
            skPoint(sketch, "E222.endSnap0", {"position": v(6.22, 57) * mm});
            skPoint(sketch, "E223", {"position": v(6.22, 28.51) * mm});
            skLineSegment(sketch, "E224.bottom", {"start": v(-4.78, 53.51) * mm, "end": v(17.22, 53.51) * mm});
            skLineSegment(sketch, "E224.top", {"start": v(-4.78, 3.51) * mm, "end": v(17.22, 3.51) * mm});
            skLineSegment(sketch, "E224.left", {"start": v(-4.78, 53.51) * mm, "end": v(-4.78, 3.51) * mm});
            skLineSegment(sketch, "E224.right", {"start": v(17.22, 53.51) * mm, "end": v(17.22, 3.51) * mm});
            skSolve(sketch);
        }
        {
            var Q0;
            Q0=makeQuery(id+"F23.imprint","IMPRINT",FACE,{"disambiguationData":[TD([[makeQuery(id+"F23.imprint","IMPRINT",EDGE,{"derivedFrom":sQuery(id+"F23.wireOp",EDGE,"E224.bottom")}),-1.0]])]});
            extrude(context, id + "F24", {"entities" : qUnion([Q0]), "operationType" : NewBodyOperationType.REMOVE, "oppositeDirection" : true, "depth" : 14 * mm, "offsetDistance" : 25 * mm});
        }
        {
            var Q0;
            Q0=qCreatedBy(makeId("Top.planeOp"),FACE);
            var sketch = newSketch(context, id + "F25", { "sketchPlane" : qUnion([Q0])});
            skLineSegment(sketch, "E225.bottom", {"start": v(267.31, -95.72) * mm, "end": v(320.31, -95.72) * mm});
            skLineSegment(sketch, "E225.left", {"start": v(264.31, -98.72) * mm, "end": v(264.31, -124.22) * mm});
            skCircle(sketch, "E226", {"center": v(273.31, -102.72) * mm, "radius": 1.5 * mm});
            skLineSegment(sketch, "E227.bottom", {"start": v(276.31, -104.22) * mm, "end": v(276.31, -101.22) * mm});
            skLineSegment(sketch, "E227.top", {"start": v(279.31, -104.22) * mm, "end": v(279.31, -101.22) * mm});
            skLineSegment(sketch, "E227.left", {"start": v(276.31, -104.22) * mm, "end": v(279.31, -104.22) * mm});
            skLineSegment(sketch, "E227.right", {"start": v(276.31, -101.22) * mm, "end": v(279.31, -101.22) * mm});
            skPoint(sketch, "E228", {"position": v(276.31, -102.72) * mm});
            skLineSegment(sketch, "E229", {"start": v(273.31, -102.72) * mm, "end": v(276.31, -102.72) * mm, "construction": true});
            skLineSegment(sketch, "E230", {"start": v(273.31, -107.09) * mm, "end": v(273.31, -98.03) * mm, "construction": true});
            skPoint(sketch, "E231.MirrorP", {"position": v(270.31, -102.72) * mm});
            skLineSegment(sketch, "E232.MirrorCS", {"start": v(270.31, -104.22) * mm, "end": v(270.31, -101.22) * mm});
            skLineSegment(sketch, "E233.MirrorCS", {"start": v(267.31, -104.22) * mm, "end": v(267.31, -101.22) * mm});
            skLineSegment(sketch, "E234.MirrorCS", {"start": v(270.31, -104.22) * mm, "end": v(267.31, -104.22) * mm});
            skLineSegment(sketch, "E235.MirrorCS", {"start": v(270.31, -101.22) * mm, "end": v(267.31, -101.22) * mm});
            skLineSegment(sketch, "E236", {"start": v(264.31, -124.22) * mm, "end": v(376.31, -124.22) * mm, "construction": true});
            skLineSegment(sketch, "E237", {"start": v(320.31, -148.72) * mm, "end": v(320.31, -95.72) * mm, "construction": true});
            skPoint(sketch, "E238.visualSharp", {"position": v(264.31, -95.72) * mm});
            skArc(sketch, "E238.filletArc", {"start": v(267.31, -95.72) * mm, "mid": v(265.19, -96.6) * mm, "end": v(264.31, -98.72) * mm});
            skPoint(sketch, "E239.orphan", {"position": v(264.31, -152.72) * mm});
            skLineSegment(sketch, "E240.MirrorCS", {"start": v(376.31, -98.72) * mm, "end": v(376.31, -124.22) * mm});
            skLineSegment(sketch, "E241.MirrorCS", {"start": v(364.31, -104.22) * mm, "end": v(364.31, -101.22) * mm});
            skLineSegment(sketch, "E242.MirrorCS", {"start": v(370.31, -104.22) * mm, "end": v(370.31, -101.22) * mm});
            skLineSegment(sketch, "E243.MirrorCS", {"start": v(367.31, -107.09) * mm, "end": v(367.31, -98.03) * mm, "construction": true});
            skLineSegment(sketch, "E244.MirrorCS", {"start": v(367.31, -102.72) * mm, "end": v(364.31, -102.72) * mm, "construction": true});
            skLineSegment(sketch, "E245.MirrorCS", {"start": v(370.31, -101.22) * mm, "end": v(373.31, -101.22) * mm});
            skPoint(sketch, "E246.MirrorP", {"position": v(376.31, -95.72) * mm});
            skLineSegment(sketch, "E247.MirrorCS", {"start": v(373.31, -104.22) * mm, "end": v(373.31, -101.22) * mm});
            skCircle(sketch, "E248.MirrorC", {"center": v(367.31, -102.72) * mm, "radius": 1.5 * mm});
            skLineSegment(sketch, "E249.MirrorCS", {"start": v(373.31, -95.72) * mm, "end": v(320.31, -95.72) * mm});
            skLineSegment(sketch, "E250.MirrorCS", {"start": v(361.31, -104.22) * mm, "end": v(361.31, -101.22) * mm});
            skLineSegment(sketch, "E251.MirrorCS", {"start": v(364.31, -101.22) * mm, "end": v(361.31, -101.22) * mm});
            skLineSegment(sketch, "E252.MirrorCS", {"start": v(364.31, -104.22) * mm, "end": v(361.31, -104.22) * mm});
            skLineSegment(sketch, "E253.MirrorCS", {"start": v(370.31, -104.22) * mm, "end": v(373.31, -104.22) * mm});
            skPoint(sketch, "E254.MirrorP", {"position": v(364.31, -102.72) * mm});
            skPoint(sketch, "E255.MirrorP", {"position": v(370.31, -102.72) * mm});
            skArc(sketch, "E256.MirrorCS", {"start": v(373.31, -95.72) * mm, "mid": v(375.43, -96.6) * mm, "end": v(376.31, -98.72) * mm});
            skLineSegment(sketch, "E257.MirrorCS", {"start": v(364.31, -144.22) * mm, "end": v(364.31, -147.22) * mm});
            skLineSegment(sketch, "E258.MirrorCS", {"start": v(276.31, -144.22) * mm, "end": v(276.31, -147.22) * mm});
            skLineSegment(sketch, "E259.MirrorCS", {"start": v(367.31, -145.72) * mm, "end": v(364.31, -145.72) * mm, "construction": true});
            skLineSegment(sketch, "E260.MirrorCS", {"start": v(364.31, -147.22) * mm, "end": v(361.31, -147.22) * mm});
            skLineSegment(sketch, "E261.MirrorCS", {"start": v(370.31, -144.22) * mm, "end": v(370.31, -147.22) * mm});
            skLineSegment(sketch, "E262.MirrorCS", {"start": v(270.31, -144.22) * mm, "end": v(270.31, -147.22) * mm});
            skLineSegment(sketch, "E263.MirrorCS", {"start": v(270.31, -147.22) * mm, "end": v(267.31, -147.22) * mm});
            skLineSegment(sketch, "E264.MirrorCS", {"start": v(276.31, -144.22) * mm, "end": v(279.31, -144.22) * mm});
            skLineSegment(sketch, "E265.MirrorCS", {"start": v(273.31, -145.72) * mm, "end": v(276.31, -145.72) * mm, "construction": true});
            skLineSegment(sketch, "E266.MirrorCS", {"start": v(367.31, -141.35) * mm, "end": v(367.31, -150.41) * mm, "construction": true});
            skLineSegment(sketch, "E267.MirrorCS", {"start": v(273.31, -141.35) * mm, "end": v(273.31, -150.41) * mm, "construction": true});
            skLineSegment(sketch, "E268.MirrorCS", {"start": v(373.31, -152.72) * mm, "end": v(320.31, -152.72) * mm});
            skArc(sketch, "E269.MirrorCS", {"start": v(373.31, -152.72) * mm, "mid": v(375.43, -151.84) * mm, "end": v(376.31, -149.72) * mm});
            skLineSegment(sketch, "E270.MirrorCS", {"start": v(279.31, -144.22) * mm, "end": v(279.31, -147.22) * mm});
            skPoint(sketch, "E271.MirrorP", {"position": v(370.31, -145.72) * mm});
            skPoint(sketch, "E272.MirrorP", {"position": v(270.31, -145.72) * mm});
            skLineSegment(sketch, "E273.MirrorCS", {"start": v(267.31, -144.22) * mm, "end": v(267.31, -147.22) * mm});
            skPoint(sketch, "E274.MirrorP", {"position": v(376.31, -152.72) * mm});
            skLineSegment(sketch, "E275.MirrorCS", {"start": v(276.31, -147.22) * mm, "end": v(279.31, -147.22) * mm});
            skCircle(sketch, "E276.MirrorC", {"center": v(367.31, -145.72) * mm, "radius": 1.5 * mm});
            skLineSegment(sketch, "E277.MirrorCS", {"start": v(376.31, -149.72) * mm, "end": v(376.31, -124.22) * mm});
            skArc(sketch, "E278.MirrorCS", {"start": v(267.31, -152.72) * mm, "mid": v(265.19, -151.84) * mm, "end": v(264.31, -149.72) * mm});
            skPoint(sketch, "E279.MirrorP", {"position": v(276.31, -145.72) * mm});
            skPoint(sketch, "E280.MirrorP", {"position": v(364.31, -145.72) * mm});
            skLineSegment(sketch, "E281.MirrorCS", {"start": v(361.31, -144.22) * mm, "end": v(361.31, -147.22) * mm});
            skLineSegment(sketch, "E282.MirrorCS", {"start": v(370.31, -144.22) * mm, "end": v(373.31, -144.22) * mm});
            skCircle(sketch, "E283.MirrorC", {"center": v(273.31, -145.72) * mm, "radius": 1.5 * mm});
            skLineSegment(sketch, "E284.MirrorCS", {"start": v(373.31, -144.22) * mm, "end": v(373.31, -147.22) * mm});
            skLineSegment(sketch, "E285.MirrorCS", {"start": v(267.31, -152.72) * mm, "end": v(320.31, -152.72) * mm});
            skLineSegment(sketch, "E286.MirrorCS", {"start": v(370.31, -147.22) * mm, "end": v(373.31, -147.22) * mm});
            skLineSegment(sketch, "E287.MirrorCS", {"start": v(364.31, -144.22) * mm, "end": v(361.31, -144.22) * mm});
            skLineSegment(sketch, "E288.MirrorCS", {"start": v(264.31, -149.72) * mm, "end": v(264.31, -124.22) * mm});
            skLineSegment(sketch, "E289.MirrorCS", {"start": v(270.31, -144.22) * mm, "end": v(267.31, -144.22) * mm});
            skLineSegment(sketch, "E290", {"start": v(304.31, -95.72) * mm, "end": v(304.31, -152.72) * mm, "construction": true});
            skLineSegment(sketch, "E291", {"start": v(336.31, -95.72) * mm, "end": v(336.31, -152.72) * mm, "construction": true});
            skCircle(sketch, "E292", {"center": v(305.31, -109.22) * mm, "radius": 1.5 * mm});
            skCircle(sketch, "E293.MirrorC", {"center": v(335.31, -109.22) * mm, "radius": 1.5 * mm});
            skCircle(sketch, "E294.MirrorC", {"center": v(335.31, -139.22) * mm, "radius": 1.5 * mm});
            skCircle(sketch, "E295.MirrorC", {"center": v(305.31, -139.22) * mm, "radius": 1.5 * mm});
            skSolve(sketch);
        }
        {
            var Q0;
            Q0=makeQuery(id+"F25.imprint","IMPRINT",FACE,{"disambiguationData":[TD([[makeQuery(id+"F25.imprint","IMPRINT",EDGE,{"derivedFrom":sQuery(id+"F25.wireOp",EDGE,"E225.bottom")}),-1.0]])]});
            extrude(context, id + "F26", {"entities" : qUnion([Q0]), "depth" : 3 * mm, "offsetDistance" : 25 * mm});
        }
        {
            var Q0;
            Q0=qCreatedBy(makeId("Top.planeOp"),FACE);
            var sketch = newSketch(context, id + "F27", { "sketchPlane" : qUnion([Q0])});
            skLineSegment(sketch, "E296.0", {"start": v(388.33, -293.55) * mm, "end": v(388.33, -243.05) * mm});
            skLineSegment(sketch, "E296.1", {"start": v(385.33, -296.55) * mm, "end": v(318.33, -296.55) * mm});
            skLineSegment(sketch, "E296.2", {"start": v(315.33, -293.55) * mm, "end": v(315.33, -243.05) * mm});
            skLineSegment(sketch, "E296.3", {"start": v(385.33, -240.05) * mm, "end": v(318.33, -240.05) * mm});
            skPoint(sketch, "E297.visualSharp", {"position": v(315.33, -240.05) * mm});
            skArc(sketch, "E297.filletArc", {"start": v(318.33, -240.05) * mm, "mid": v(316.21, -240.93) * mm, "end": v(315.33, -243.05) * mm});
            skPoint(sketch, "E298.visualSharp", {"position": v(315.33, -296.55) * mm});
            skArc(sketch, "E298.filletArc", {"start": v(315.33, -293.55) * mm, "mid": v(316.21, -295.67) * mm, "end": v(318.33, -296.55) * mm});
            skPoint(sketch, "E299.visualSharp", {"position": v(388.33, -240.05) * mm});
            skArc(sketch, "E299.filletArc", {"start": v(388.33, -243.05) * mm, "mid": v(387.45, -240.93) * mm, "end": v(385.33, -240.05) * mm});
            skPoint(sketch, "E300.visualSharp", {"position": v(388.33, -296.55) * mm});
            skArc(sketch, "E300.filletArc", {"start": v(385.33, -296.55) * mm, "mid": v(387.45, -295.67) * mm, "end": v(388.33, -293.55) * mm});
            skLineSegment(sketch, "E301.bottom", {"start": v(336.83, -253.3) * mm, "end": v(366.83, -253.3) * mm, "construction": true});
            skLineSegment(sketch, "E301.top", {"start": v(336.83, -283.3) * mm, "end": v(366.83, -283.3) * mm, "construction": true});
            skLineSegment(sketch, "E301.left", {"start": v(336.83, -253.3) * mm, "end": v(336.83, -283.3) * mm, "construction": true});
            skLineSegment(sketch, "E301.right", {"start": v(366.83, -253.3) * mm, "end": v(366.83, -283.3) * mm, "construction": true});
            skCircle(sketch, "E302", {"center": v(336.83, -253.3) * mm, "radius": 1.5 * mm});
            skCircle(sketch, "E303", {"center": v(366.83, -253.3) * mm, "radius": 1.5 * mm});
            skCircle(sketch, "E304", {"center": v(366.83, -283.3) * mm, "radius": 1.5 * mm});
            skCircle(sketch, "E305", {"center": v(336.83, -283.3) * mm, "radius": 1.5 * mm});
            skPoint(sketch, "E306", {"position": v(351.83, -268.3) * mm});
            skPoint(sketch, "E307.positionSnap0", {"position": v(351.83, -253.3) * mm});
            skPoint(sketch, "E307.positionSnap1", {"position": v(336.83, -268.3) * mm});
            skCircle(sketch, "E308.0", {"center": v(373.18, -293.13) * mm, "radius": 1.59 * mm});
            skCircle(sketch, "E309.0", {"center": v(321.11, -288.05) * mm, "radius": 1.59 * mm});
            skCircle(sketch, "E310.0", {"center": v(321.11, -260.11) * mm, "radius": 1.59 * mm});
            skCircle(sketch, "E311.0", {"center": v(371.91, -244.87) * mm, "radius": 1.59 * mm});
            skLineSegment(sketch, "E312.bottom", {"start": v(387.15, -295.67) * mm, "end": v(387.15, -242.33) * mm, "construction": true});
            skLineSegment(sketch, "E312.top", {"start": v(318.33, -295.67) * mm, "end": v(318.33, -242.33) * mm, "construction": true});
            skLineSegment(sketch, "E312.left", {"start": v(387.15, -295.67) * mm, "end": v(318.33, -295.67) * mm, "construction": true});
            skLineSegment(sketch, "E312.right", {"start": v(387.15, -242.33) * mm, "end": v(318.33, -242.33) * mm, "construction": true});
            skPoint(sketch, "E313", {"position": v(316.21, -295.67) * mm});
            skSolve(sketch);
        }
        {
            var Q0;
            Q0=makeQuery(id+"F27.imprint","IMPRINT",FACE,{"disambiguationData":[TD([[makeQuery(id+"F27.imprint","IMPRINT",EDGE,{"derivedFrom":sQuery(id+"F27.wireOp",EDGE,"E296.0")}),1.0]])]});
            extrude(context, id + "F28", {"entities" : qUnion([Q0]), "depth" : 3 * mm, "offsetDistance" : 25 * mm});
        }
    });
